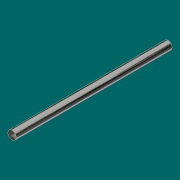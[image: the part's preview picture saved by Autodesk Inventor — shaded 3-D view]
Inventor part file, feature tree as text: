
AUTODESK INVENTOR PART (.ipt)
format: ipt  version: 2017 (Build 210142000, 142)  size: 71,168 bytes
history: native  units: in
note: dims shown in document units (in); Inventor stores cm internally (conversion verified against a paired STEP export)
features: extrude x1, sketch x1
ambient origin geometry x8: Origin, YZ Plane, XZ Plane, XY Plane, X Axis, Y Axis, Z Axis, Center Point
bodies: Solid1 (feature_tree)
feature tree (2):
  extrude  "Extrusion1"  Depth=42.0in TaperAngle=0.0deg
  sketch  "Sketch1"  dims[d0=2.25in d1=42.0in d2=0.0in]
